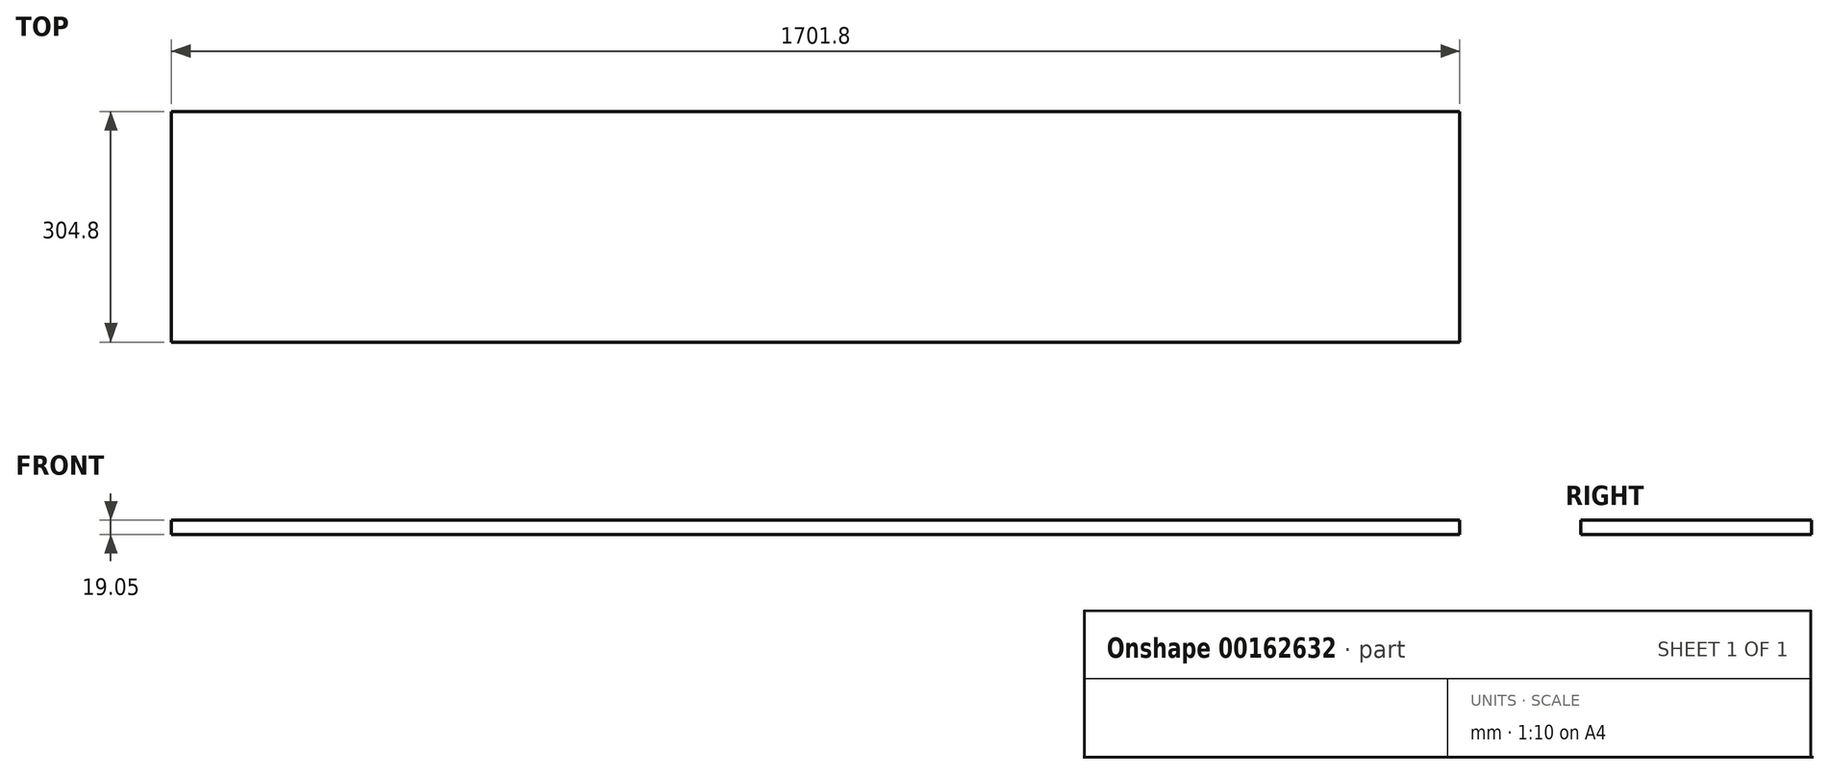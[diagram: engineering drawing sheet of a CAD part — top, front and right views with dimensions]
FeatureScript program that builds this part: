
annotation { "Feature Type Name" : "Feature", "Feature Type Description" : "" }
export const myFeature = defineFeature(function(context is Context, id is Id, definition is map)
    precondition{}
    {
        {
            var Q0;
            Q0=qCreatedBy(makeId("Top.planeOp"),FACE);
            var sketch = newSketch(context, id + "F0", { "sketchPlane" : qUnion([Q0])});
            skLineSegment(sketch, "E0.bottom", {"start": v(-141.34, 235.45) * mm, "end": v(1560.46, 235.45) * mm});
            skLineSegment(sketch, "E0.top", {"start": v(-141.34, -69.35) * mm, "end": v(1560.46, -69.35) * mm});
            skLineSegment(sketch, "E0.left", {"start": v(-141.34, 235.45) * mm, "end": v(-141.34, -69.35) * mm});
            skLineSegment(sketch, "E0.right", {"start": v(1560.46, 235.45) * mm, "end": v(1560.46, -69.35) * mm});
            skSolve(sketch);
        }
        {
            var Q0;
            Q0 = qSketchRegion(id + "F0", true);
            extrude(context, id + "F1", {"entities" : qUnion([Q0]), "depth" : 19.05 * mm});
        }
    });
